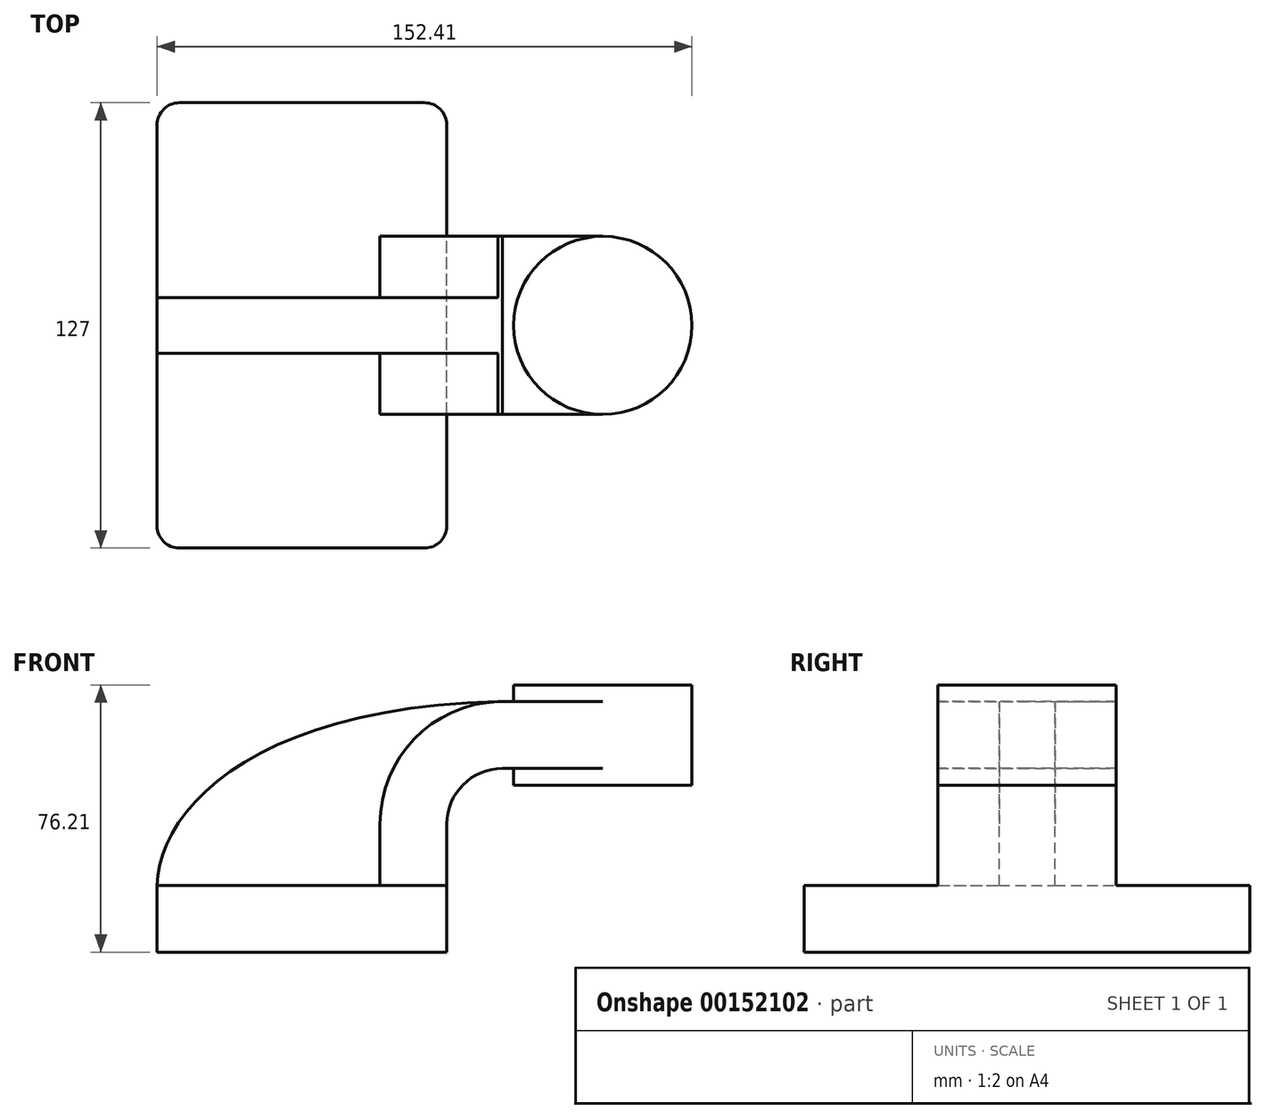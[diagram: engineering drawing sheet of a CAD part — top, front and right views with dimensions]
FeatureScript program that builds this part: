
annotation { "Feature Type Name" : "Feature", "Feature Type Description" : "" }
export const myFeature = defineFeature(function(context is Context, id is Id, definition is map)
    precondition{}
    {
        {
            var Q0;
            Q0=qCreatedBy(makeId("Front.planeOp"),FACE);
            var sketch = newSketch(context, id + "F0", { "sketchPlane" : qUnion([Q0])});
            skLineSegment(sketch, "E0.bottom", {"start": v(41.27, 9.53) * mm, "end": v(-41.27, 9.53) * mm});
            skLineSegment(sketch, "E0.top", {"start": v(41.28, -9.52) * mm, "end": v(-41.27, -9.52) * mm});
            skLineSegment(sketch, "E0.left", {"start": v(41.28, 9.53) * mm, "end": v(41.28, -9.52) * mm});
            skLineSegment(sketch, "E0.right", {"start": v(-41.27, 9.53) * mm, "end": v(-41.27, -9.52) * mm});
            skPoint(sketch, "E0.middle", {"position": v(0, 0) * mm});
            skLineSegment(sketch, "E1.bottom", {"start": v(60.32, 38.1) * mm, "end": v(111.12, 38.1) * mm});
            skLineSegment(sketch, "E1.top", {"start": v(60.32, 66.68) * mm, "end": v(111.12, 66.68) * mm});
            skLineSegment(sketch, "E1.left", {"start": v(60.32, 38.1) * mm, "end": v(60.32, 66.68) * mm});
            skLineSegment(sketch, "E1.right", {"start": v(111.12, 38.1) * mm, "end": v(111.12, 66.68) * mm});
            skPoint(sketch, "E1.middle", {"position": v(85.72, 52.39) * mm});
            skLineSegment(sketch, "E2", {"start": v(41.27, 9.53) * mm, "end": v(41.27, 26.99) * mm});
            skArc(sketch, "E3", {"start": v(41.27, 26.99) * mm, "mid": v(45.92, 38.21) * mm, "end": v(57.15, 42.86) * mm});
            skLineSegment(sketch, "E4", {"start": v(57.15, 42.86) * mm, "end": v(85.72, 42.86) * mm});
            skLineSegment(sketch, "E5.0", {"start": v(57.15, 61.91) * mm, "end": v(85.72, 61.91) * mm});
            skArc(sketch, "E5.1", {"start": v(22.22, 26.99) * mm, "mid": v(32.45, 51.68) * mm, "end": v(57.15, 61.91) * mm});
            skLineSegment(sketch, "E5.2", {"start": v(22.22, 9.53) * mm, "end": v(22.22, 26.99) * mm});
            skLineSegment(sketch, "E6", {"start": v(85.73, 38.1) * mm, "end": v(85.72, 42.86) * mm});
            skLineSegment(sketch, "E7", {"start": v(85.72, 42.86) * mm, "end": v(85.72, 61.91) * mm});
            skLineSegment(sketch, "E8", {"start": v(85.72, 61.91) * mm, "end": v(85.72, 66.68) * mm});
            skFitSpline(sketch, "E9", {"points": [v(-41.28, 9.52) * mm, v(57.15, 61.91) * mm], "startDerivative": vector(0.99, 65.38) * mm, "endDerivative": vector(209.58, 3.25) * mm});
            skSolve(sketch);
        }
        {
            var Q0;
            Q0=makeQuery(id+"F0.imprint","IMPRINT",FACE,{"disambiguationData":[TD([[makeQuery(id+"F0.imprint","IMPRINT",EDGE,{"derivedFrom":sQuery(id+"F0.wireOp",EDGE,"E0.top")}),-1.0]])]});
            extrude(context, id + "F1", {"entities" : qUnion([Q0]), "endBound" : BoundingType.SYMMETRIC, "depth" : 127 * mm});
        }
        {
            var Q0;
            {var subQ1=sQuery(id+"F0.wireOp",EDGE,"E2");Q0=makeQuery(id+"F0.imprint","IMPRINT",FACE,{"disambiguationData":[TD([[makeQuery(id+"F0.imprint","IMPRINT",EDGE,{"derivedFrom":subQ1}),1.0]])]});}
            var Q1;
            {var subQ5=sQuery(id+"F0.wireOp",EDGE,"E7");Q1=makeQuery(id+"F0.imprint","IMPRINT",FACE,{"disambiguationData":[TD([[makeQuery(id+"F0.imprint","IMPRINT",EDGE,{"derivedFrom":subQ5}),1.0]])]});}
            extrude(context, id + "F2", {"entities" : qUnion([Q0, Q1]), "operationType" : NewBodyOperationType.ADD, "endBound" : BoundingType.SYMMETRIC, "depth" : 50.8 * mm});
        }
        {
            var Q0;
            {var subQ3=sQuery(id+"F0.wireOp",EDGE,"E5.2");Q0=makeQuery(id+"F0.imprint","IMPRINT",FACE,{"disambiguationData":[TD([[makeQuery(id+"F0.imprint","IMPRINT",EDGE,{"derivedFrom":subQ3}),1.0]])]});}
            extrude(context, id + "F3", {"entities" : qUnion([Q0]), "operationType" : NewBodyOperationType.ADD, "endBound" : BoundingType.SYMMETRIC, "depth" : 15.88 * mm});
        }
        {
            var Q0;
            {var subQ0=sQuery(id+"F0.wireOp",EDGE,"E1.right");Q0=makeQuery(id+"F0.imprint","IMPRINT",FACE,{"disambiguationData":[TD([[makeQuery(id+"F0.imprint","IMPRINT",EDGE,{"derivedFrom":subQ0}),1.0]])]});}
            var Q1;
            Q1=sQuery(id+"F0.wireOp",EDGE,"E7");
            revolve(context, id + "F4", {"operationType" : NewBodyOperationType.ADD, "entities" : qUnion([Q0]), "axis" : qUnion([Q1]), "revolveType" : RevolveType.FULL});
        }
        {
            var Q0;
            Q0=makeQuery(id+"F1.opExtrude","CAP_EDGE",EDGE,{"disambiguationData":[OSD([sQuery(id+"F0.wireOp",EDGE,"E0.left")])],"isStart":false});
            var Q1;
            Q1=makeQuery(id+"F1.opExtrude","CAP_EDGE",EDGE,{"disambiguationData":[OSD([sQuery(id+"F0.wireOp",EDGE,"E0.right")])],"isStart":false});
            var Q2;
            Q2=makeQuery(id+"F1.opExtrude","CAP_EDGE",EDGE,{"disambiguationData":[OSD([sQuery(id+"F0.wireOp",EDGE,"E0.left")])],"isStart":true});
            var Q3;
            Q3=makeQuery(id+"F1.opExtrude","CAP_EDGE",EDGE,{"disambiguationData":[OSD([sQuery(id+"F0.wireOp",EDGE,"E0.right")])],"isStart":true});
            fillet(context, id + "F5", {"entities" : qUnion([Q0, Q1, Q2, Q3]), "radius" : 6.35 * mm, "tangentPropagation" : true, "allowEdgeOverflow" : false});
        }
    });
